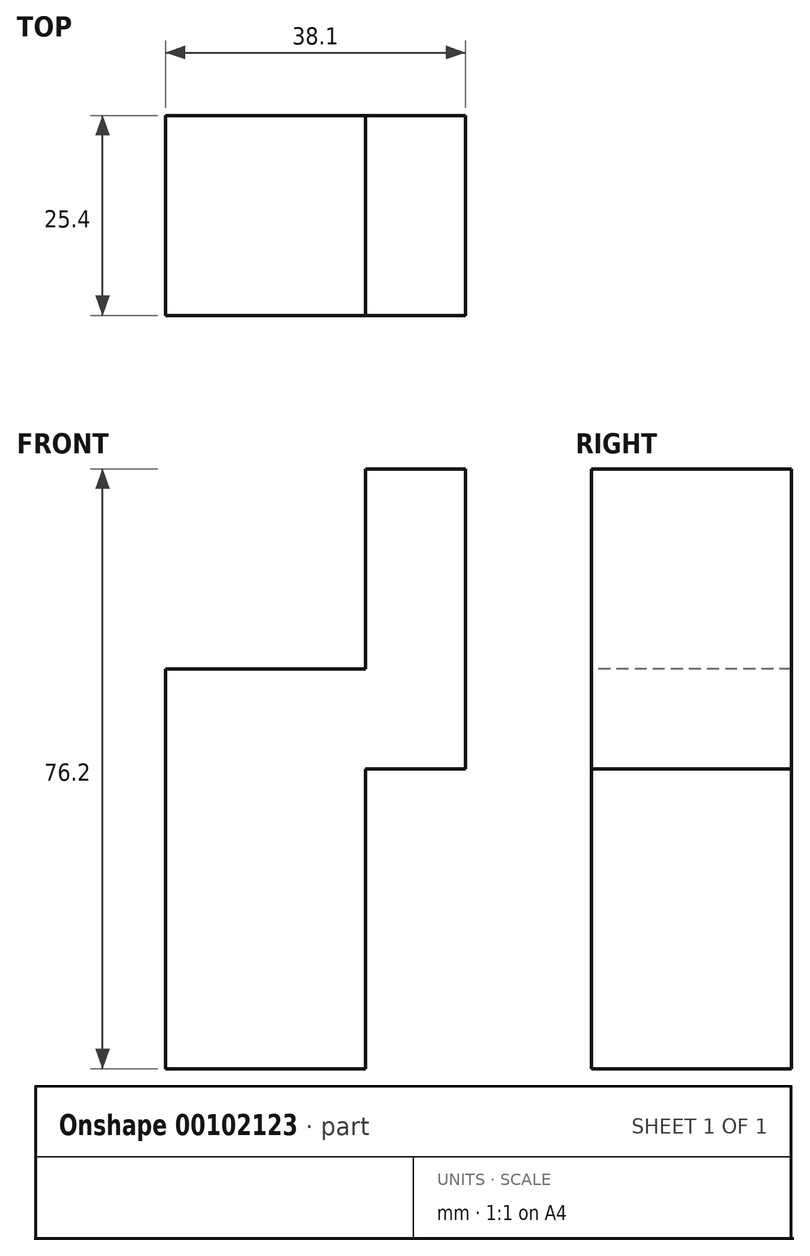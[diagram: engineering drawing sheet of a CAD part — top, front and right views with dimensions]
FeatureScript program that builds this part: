
annotation { "Feature Type Name" : "Feature", "Feature Type Description" : "" }
export const myFeature = defineFeature(function(context is Context, id is Id, definition is map)
    precondition{}
    {
        {
            var Q0;
            Q0=qCreatedBy(makeId("Top.planeOp"),FACE);
            var sketch = newSketch(context, id + "F0", { "sketchPlane" : qUnion([Q0])});
            skLineSegment(sketch, "E0.bottom", {"start": v(-11.39, 9) * mm, "end": v(14.01, 9) * mm});
            skLineSegment(sketch, "E0.top", {"start": v(-11.39, -16.4) * mm, "end": v(14.01, -16.4) * mm});
            skLineSegment(sketch, "E0.left", {"start": v(-11.39, 9) * mm, "end": v(-11.39, -16.4) * mm});
            skLineSegment(sketch, "E0.right", {"start": v(14.01, 9) * mm, "end": v(14.01, -16.4) * mm});
            skSolve(sketch);
        }
        {
            var Q0;
            Q0 = qSketchRegion(id + "F0", true);
            extrude(context, id + "F1", {"entities" : qUnion([Q0]), "depth" : 50.8 * mm});
        }
        {
            var Q0;
            Q0=makeQuery(id+"F1.opExtrude","SWEPT_FACE",FACE,{"disambiguationData":[OSD([sQuery(id+"F0.wireOp",EDGE,"E0.right")])]});
            var sketch = newSketch(context, id + "F2", { "sketchPlane" : qUnion([Q0])});
            skLineSegment(sketch, "E1.bottom", {"start": v(-16.4, 50.8) * mm, "end": v(9, 50.8) * mm});
            skLineSegment(sketch, "E1.top", {"start": v(-16.4, 38.1) * mm, "end": v(9, 38.1) * mm});
            skLineSegment(sketch, "E1.left", {"start": v(-16.4, 50.8) * mm, "end": v(-16.4, 38.1) * mm});
            skLineSegment(sketch, "E1.right", {"start": v(9, 50.8) * mm, "end": v(9, 38.1) * mm});
            skSolve(sketch);
        }
        {
            var Q0;
            Q0 = qSketchRegion(id + "F2", true);
            extrude(context, id + "F3", {"entities" : qUnion([Q0]), "operationType" : NewBodyOperationType.ADD, "depth" : 12.7 * mm});
        }
        {
            var Q0;
            Q0=makeQuery(id+"F3.boolean.opBoolean","MERGE",FACE,{"derivedFrom":[makeQuery(id+"F1.opExtrude","CAP_FACE",FACE,{"disambiguationData":[OSD([sQuery(id+"F0.wireOp",EDGE,"E0.bottom"),sQuery(id+"F0.wireOp",EDGE,"E0.top"),sQuery(id+"F0.wireOp",EDGE,"E0.left"),sQuery(id+"F0.wireOp",EDGE,"E0.right")])],"isStart":false}),makeQuery(id+"F3.opExtrude","SWEPT_FACE",FACE,{"disambiguationData":[OSD([sQuery(id+"F2.wireOp",EDGE,"E1.bottom")])]})]});
            var sketch = newSketch(context, id + "F4", { "sketchPlane" : qUnion([Q0])});
            skLineSegment(sketch, "E2.bottom", {"start": v(14.01, 9) * mm, "end": v(26.71, 9) * mm});
            skLineSegment(sketch, "E2.top", {"start": v(14.01, -16.4) * mm, "end": v(26.71, -16.4) * mm});
            skLineSegment(sketch, "E2.left", {"start": v(14.01, 9) * mm, "end": v(14.01, -16.4) * mm});
            skLineSegment(sketch, "E2.right", {"start": v(26.71, 9) * mm, "end": v(26.71, -16.4) * mm});
            skSolve(sketch);
        }
        {
            var Q0;
            Q0 = qSketchRegion(id + "F4", true);
            extrude(context, id + "F5", {"entities" : qUnion([Q0]), "operationType" : NewBodyOperationType.ADD, "depth" : 25.4 * mm});
        }
    });
